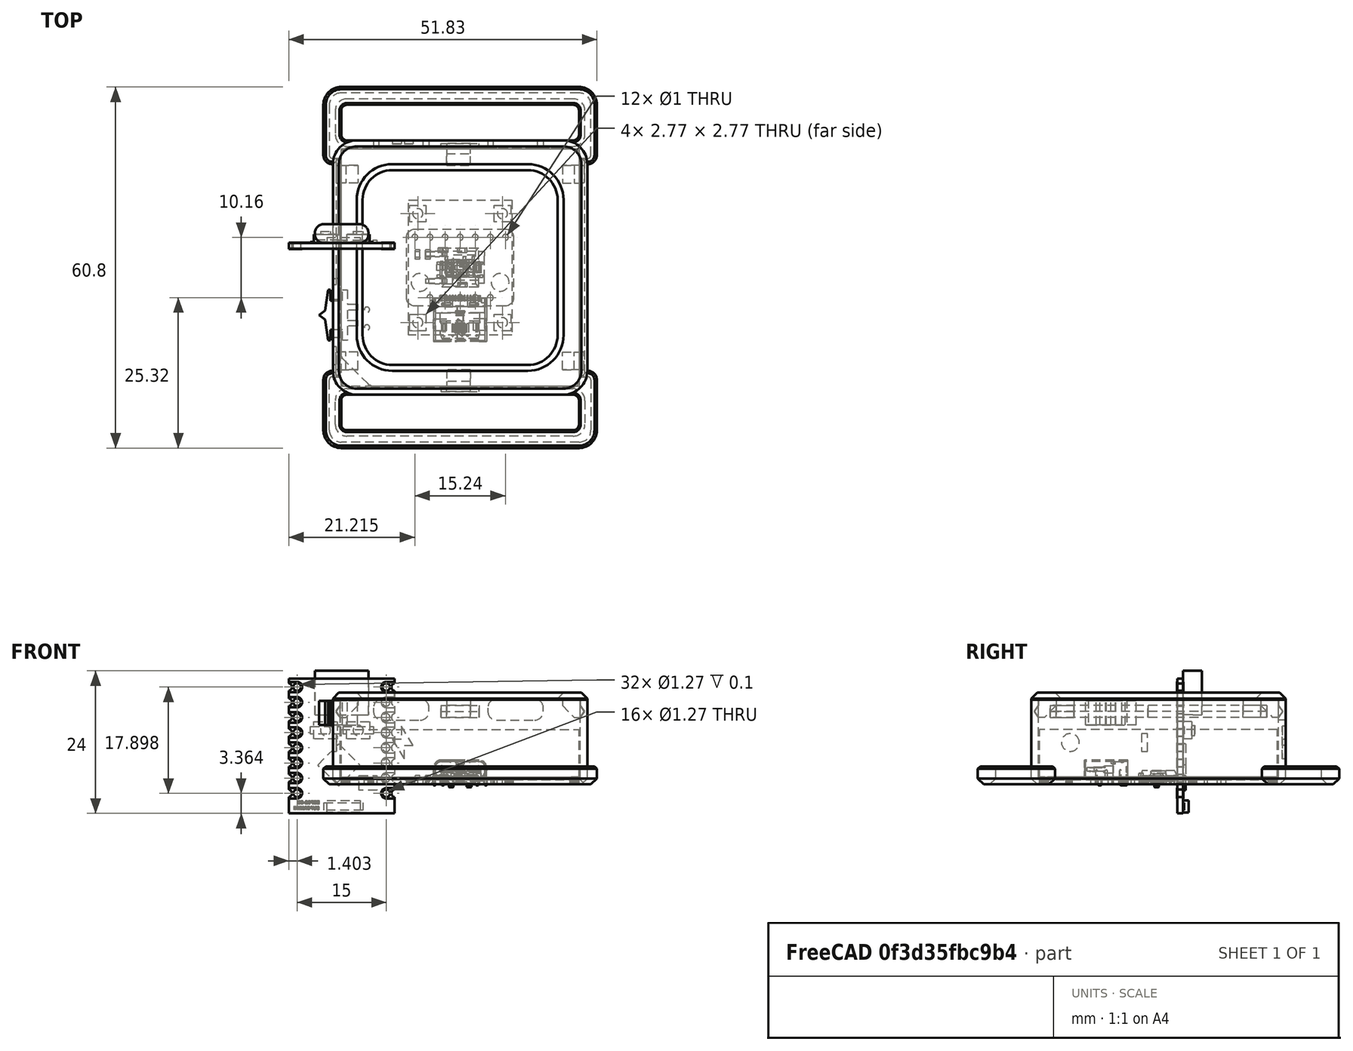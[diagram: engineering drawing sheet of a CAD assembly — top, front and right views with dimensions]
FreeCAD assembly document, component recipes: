
FREECAD ASSEMBLY — COMPONENT RECIPES ("tiny-slime-case")

This assembly document has 5 components, labeled P0..P4 below (a component is one placed body or linked part). 4 of them carry a construction recipe — the FreeCAD feature program that regenerates the part from scratch, quoted from this document or its linked companion documents; the rest are supplied as boundary geometry only. No exploded tour is included for this assembly.
COMPONENT P0 — recipe-attached ("Battery", modeled in this document).
Construction recipe (the document's own serialized feature program — sketch geometry with constraints, then the solid features built on it; lengths are millimeters unless a unit is written):

FEATURE [Sketcher::SketchObject] Sketch
  ArcFitTolerance = 1e-06
  AttachmentSupport = -> [XY_Plane]
  ExternalBSplineMaxDegree = 5
  ExternalBSplineTolerance = 0.0001
  FullyConstrained = true
  InternalTolerance = 1e-06
  InvalidShape = false
  MakeInternals = false
  MapMode = 5
  Support = -> [XY_Plane]
  TreeRank = 50
  ValidateShape = false
  sketch-geometry (4):
    g0: LineSegment StartX=-20 StartY=20 StartZ=0 EndX=20 EndY=20 EndZ=0
    g1: LineSegment StartX=20 StartY=20 StartZ=0 EndX=20 EndY=-20 EndZ=0
    g2: LineSegment StartX=20 StartY=-20 StartZ=0 EndX=-20 EndY=-20 EndZ=0
    g3: LineSegment StartX=-20 StartY=-20 StartZ=0 EndX=-20 EndY=20 EndZ=0
  constraints (11):
    c: Coincident(g0,g1)
    c: Coincident(g1,g2)
    c: Coincident(g2,g3)
    c: Coincident(g3,g0)
    c: Horizontal(g0)
    c: Horizontal(g2)
    c: Vertical(g1)
    c: Vertical(g3)
    c: DistanceY(g1,g1) = 40
    c: Equal(g1,g2)
    c: Symmetric(g1,g0,g-1)
FEATURE [PartDesign::Pad] Pad
  AddSubType = 0
  AlongSketchNormal = false
  AutoTaperInnerAngle = true
  CheckUpToFaceLimits = true
  ClaimChildren = false
  Direction = (0,0,1)
  Fit = 0
  FitJoin = 0
  InnerFit = 0
  InnerFitJoin = 0
  InvalidShape = false
  Length = 8
  Length2 = 10
  Linearize = true
  NewSolid = false
  Profile = -> Sketch
  ReferenceAxis = -> Sketch [N_Axis]
  Suppress = false
  TaperInnerAngle = 0
  TaperInnerAngleRev = 0
  TreeRank = 51
  Type = 0
  ValidateShape = false
  _ProfileBasedVersion = 1
FEATURE [PartDesign::Body] Body  label="Battery"
  AutoGroupSolids = false
  ClaimAllChildren = false
  ExportMode = 0
  Group = -> [Sketch,Pad]
  InvalidShape = false
  Origin = -> Origin008
  Placement = pos=(0,0,1.2) rot=(0,0,1;0rad)
  Tip = -> Pad
  TreeRank = 49
  ValidateShape = false
  _ExportChildren = -> [Pad]
  _GroupVersion = 1
COMPONENT P1 — recipe-attached ("Bottom", modeled in this document).
Construction recipe (the document's own serialized feature program — sketch geometry with constraints, then the solid features built on it; lengths are millimeters unless a unit is written):

FEATURE [Part::SubShapeBinder] Import  label="Import(Pad)"
  BindCopyOnChange = 0
  BindMode = 0
  ClaimChildren = false
  Context = -> Body001 [Import.]
  EdgeTolerance = 1e-06
  FillStyle = 0
  Fuse = false
  InvalidShape = false
  MakeFace = false
  MergeEdges = true
  OffsetFill = false
  OffsetIntersection = false
  OffsetJoinType = 0
  OffsetOpenResult = false
  Outline = false
  PartialLoad = false
  Relative = true
  SplitEdges = false
  Support = -> [Body[Pad.]]
  TightBound = false
  TreeRank = 62
  ValidateShape = false
  _Version = 8
FEATURE [Sketcher::SketchObject] Sketch001
  ArcFitTolerance = 1e-06
  AttachmentSupport = -> [Import]
  ExternalBSplineMaxDegree = 5
  ExternalBSplineTolerance = 0.0001
  ExternalGeometry = -> [Import]
  FullyConstrained = true
  InternalTolerance = 1e-06
  InvalidShape = false
  MakeInternals = false
  MapMode = 5
  Placement = pos=(0,0,1.2) rot=(1,0,0;3.14159rad)
  Support = -> [Import]
  TreeRank = 63
  ValidateShape = false
  sketch-geometry (4):
    g0: LineSegment StartX=-21.4 StartY=21.4 StartZ=0 EndX=21.4 EndY=21.4 EndZ=0
    g1: LineSegment StartX=21.4 StartY=21.4 StartZ=0 EndX=21.4 EndY=-21.4 EndZ=0
    g2: LineSegment StartX=21.4 StartY=-21.4 StartZ=0 EndX=-21.4 EndY=-21.4 EndZ=0
    g3: LineSegment StartX=-21.4 StartY=-21.4 StartZ=0 EndX=-21.4 EndY=21.4 EndZ=0
  constraints (11):
    c: Coincident(g0,g1)
    c: Coincident(g1,g2)
    c: Coincident(g2,g3)
    c: Coincident(g3,g0)
    c: Horizontal(g0)
    c: Horizontal(g2)
    c: Vertical(g1)
    c: Vertical(g3)
    c: Symmetric(g1,g0,g-1)
    c: Equal(g1,g0)
    c: DistanceY(g-3,g0) = 1.4
FEATURE [PartDesign::Pad] Pad001
  AddSubType = 0
  AlongSketchNormal = false
  AutoTaperInnerAngle = true
  CheckUpToFaceLimits = true
  ClaimChildren = false
  Direction = (0,0,-1)
  Fit = 0
  FitJoin = 0
  InnerFit = 0
  InnerFitJoin = 0
  InvalidShape = false
  Length = 1.2
  Length2 = 10
  Linearize = true
  NewSolid = false
  Profile = -> Sketch001
  ReferenceAxis = -> Sketch001 [N_Axis]
  Suppress = false
  TaperInnerAngle = 0
  TaperInnerAngleRev = 0
  TreeRank = 64
  Type = 0
  ValidateShape = false
  _ProfileBasedVersion = 1
FEATURE [Sketcher::SketchObject] Sketch002
  ArcFitTolerance = 1e-06
  AttachmentSupport = -> [Pad001]
  ExternalBSplineMaxDegree = 5
  ExternalBSplineTolerance = 0.0001
  ExternalGeometry = -> [Pad001]
  FullyConstrained = true
  InternalTolerance = 1e-06
  InvalidShape = false
  MakeInternals = false
  MapMode = 5
  Placement = pos=(0,0,1.2) rot=(0,0,1;0rad)
  Support = -> [Pad001]
  TreeRank = 65
  ValidateShape = false
  sketch-geometry (4):
    g0: LineSegment StartX=-20.2 StartY=20.2 StartZ=0 EndX=20.2 EndY=20.2 EndZ=0
    g1: LineSegment StartX=20.2 StartY=20.2 StartZ=0 EndX=20.2 EndY=-20.2 EndZ=0
    g2: LineSegment StartX=20.2 StartY=-20.2 StartZ=0 EndX=-20.2 EndY=-20.2 EndZ=0
    g3: LineSegment StartX=-20.2 StartY=-20.2 StartZ=0 EndX=-20.2 EndY=20.2 EndZ=0
  constraints (11):
    c: Coincident(g0,g1)
    c: Coincident(g1,g2)
    c: Coincident(g2,g3)
    c: Coincident(g3,g0)
    c: Horizontal(g0)
    c: Horizontal(g2)
    c: Vertical(g1)
    c: Vertical(g3)
    c: Symmetric(g1,g0,g-1)
    c: Equal(g0,g3)
    c: DistanceY(g0,g-4) = 1.2
FEATURE [PartDesign::SubShapeBinder] Import001  label="Import001(COMPOUND)"
  BindCopyOnChange = 0
  BindMode = 0
  ClaimChildren = false
  Context = -> Body001 [Import001.]
  EdgeTolerance = 1e-06
  FillStyle = 0
  Fuse = false
  InvalidShape = false
  MakeFace = false
  MergeEdges = true
  OffsetFill = false
  OffsetIntersection = false
  OffsetJoinType = 0
  OffsetOpenResult = false
  Outline = false
  PartialLoad = false
  Relative = true
  SplitEdges = false
  Support = -> [Part007[Part.Compound.Face247]]
  TightBound = false
  TreeRank = 67
  ValidateShape = false
  _Version = 8
FEATURE [PartDesign::Pad] Pad002
  AddSubType = 0
  AlongSketchNormal = false
  AutoTaperInnerAngle = true
  BaseFeature = -> Pad001
  CheckUpToFaceLimits = true
  ClaimChildren = false
  Direction = (0,0,1)
  Fit = 0
  FitJoin = 0
  InnerFit = 0
  InnerFitJoin = 0
  InvalidShape = false
  Length = 10
  Length2 = 10
  Linearize = true
  NewSolid = false
  Offset = -0.1
  Profile = -> Sketch002
  ReferenceAxis = -> Sketch002 [N_Axis]
  Suppress = false
  TaperInnerAngle = 0
  TaperInnerAngleRev = 0
  TreeRank = 66
  Type = 3
  UpToFace = -> Import001
  ValidateShape = false
  _ProfileBasedVersion = 1
FEATURE [Part::SubShapeBinder] Import002  label="Import002(COMPOUND)"
  BindCopyOnChange = 0
  BindMode = 0
  ClaimChildren = false
  Context = -> Body001 [Import002.]
  EdgeTolerance = 1e-06
  FillStyle = 0
  Fuse = false
  InvalidShape = false
  MakeFace = false
  MergeEdges = true
  OffsetFill = false
  OffsetIntersection = false
  OffsetJoinType = 0
  OffsetOpenResult = false
  Outline = false
  PartialLoad = false
  Relative = true
  SplitEdges = false
  Support = -> [Part007[Part002.Compound001.]]
  TightBound = false
  TreeRank = 69
  ValidateShape = false
  _Version = 8
FEATURE [Part::SubShapeBinder] Import003  label="Import003(COMPOUND)"
  BindCopyOnChange = 0
  BindMode = 0
  ClaimChildren = false
  Context = -> Body001 [Import003.]
  EdgeTolerance = 1e-06
  FillStyle = 0
  Fuse = false
  InvalidShape = false
  MakeFace = false
  MergeEdges = true
  OffsetFill = false
  OffsetIntersection = false
  OffsetJoinType = 0
  OffsetOpenResult = false
  Outline = false
  PartialLoad = false
  Relative = true
  SplitEdges = false
  Support = -> [Part007[Part.Compound.]]
  TightBound = false
  TreeRank = 70
  ValidateShape = false
  _Version = 8
FEATURE [Sketcher::SketchObject] Sketch003
  ArcFitTolerance = 1e-06
  AttachmentSupport = -> [Pad002]
  ExternalBSplineMaxDegree = 5
  ExternalBSplineTolerance = 0.0001
  ExternalGeometry = -> [Import002,Import003]
  FullyConstrained = true
  InternalTolerance = 1e-06
  InvalidShape = false
  MakeInternals = false
  MapMode = 5
  Placement = pos=(0,21.4,0) rot=(0,0.707107,0.707107;3.14159rad)
  Support = -> [Pad002]
  TreeRank = 68
  ValidateShape = false
  sketch-geometry (22):
    g0: ArcOfCircle CenterX=6.7254 CenterY=12.8646 CenterZ=0 NormalX=0 NormalY=0 NormalZ=1 AngleXU=0 Radius=1.4954 StartAngle=1.5708 EndAngle=3.14159
    g1: LineSegment StartX=6.7254 StartY=14.36 StartZ=0 EndX=13.0746 EndY=14.36 EndZ=0
    g2: ArcOfCircle CenterX=13.0746 CenterY=12.8646 CenterZ=0 NormalX=0 NormalY=0 NormalZ=1 AngleXU=0 Radius=1.4954 StartAngle=0 EndAngle=1.5708
    g3: LineSegment StartX=14.57 StartY=12.8646 StartZ=0 EndX=14.57 EndY=12.2954 EndZ=0
    g4: ArcOfCircle CenterX=13.0746 CenterY=12.2954 CenterZ=0 NormalX=0 NormalY=0 NormalZ=1 AngleXU=0 Radius=1.4954 StartAngle=4.71239 EndAngle=6.28319
    g5: LineSegment StartX=13.0746 StartY=10.8 StartZ=0 EndX=6.7254 EndY=10.8 EndZ=0
    g6: ArcOfCircle CenterX=6.7254 CenterY=12.2954 CenterZ=0 NormalX=0 NormalY=0 NormalZ=1 AngleXU=0 Radius=1.4954 StartAngle=3.14159 EndAngle=4.71239
    g7: LineSegment StartX=5.23 StartY=12.2954 StartZ=0 EndX=5.23 EndY=12.8646 EndZ=0
    g8: GeomPoint [constr] X=5.23 Y=14.36 Z=0
    g9: GeomPoint [constr] X=14.57 Y=10.8 Z=0
    g10: ArcOfCircle CenterX=-12.508 CenterY=12.8646 CenterZ=0 NormalX=0 NormalY=0 NormalZ=1 AngleXU=0 Radius=1.4954 StartAngle=1.5708 EndAngle=3.14159
    g11: LineSegment StartX=-12.508 StartY=14.36 StartZ=0 EndX=-6.15878 EndY=14.36 EndZ=0
    g12: ArcOfCircle CenterX=-6.15878 CenterY=12.8646 CenterZ=0 NormalX=0 NormalY=0 NormalZ=1 AngleXU=0 Radius=1.4954 StartAngle=0 EndAngle=1.5708
    g13: LineSegment StartX=-4.66338 StartY=12.8646 StartZ=0 EndX=-4.66338 EndY=12.2954 EndZ=0
    g14: ArcOfCircle CenterX=-6.15878 CenterY=12.2954 CenterZ=0 NormalX=0 NormalY=0 NormalZ=1 AngleXU=0 Radius=1.4954 StartAngle=4.71239 EndAngle=6.28319
    g15: LineSegment StartX=-6.15878 StartY=10.8 StartZ=0 EndX=-12.508 EndY=10.8 EndZ=0
    g16: ArcOfCircle CenterX=-12.508 CenterY=12.2954 CenterZ=0 NormalX=0 NormalY=0 NormalZ=1 AngleXU=0 Radius=1.4954 StartAngle=3.14159 EndAngle=4.71239
    g17: LineSegment StartX=-14.0034 StartY=12.2954 StartZ=0 EndX=-14.0034 EndY=12.8646 EndZ=0
    g18: GeomPoint [constr] X=-14.0034 Y=14.36 Z=0
    g19: GeomPoint [constr] X=-4.66338 Y=10.8 Z=0
    g20: LineSegment [constr] StartX=-18.2334 StartY=10.9 StartZ=0 EndX=-12.508 EndY=12.2954 EndZ=0
    g21: LineSegment [constr] StartX=-6.15878 StartY=12.2954 StartZ=0 EndX=-0.433383 EndY=10.9 EndZ=0
  constraints (49):
    c: Tangent(g0,g1) = 1.5708
    c: Tangent(g1,g2) = 1.5708
    c: Tangent(g2,g3) = 1.5708
    c: Tangent(g3,g4) = 1.5708
    c: Tangent(g4,g5) = 1.5708
    c: Tangent(g5,g6) = 1.5708
    c: Tangent(g6,g7) = 1.5708
    c: Tangent(g7,g0) = 1.5708
    c: Horizontal(g1)
    c: Horizontal(g5)
    c: Vertical(g3)
    c: Vertical(g7)
    c: Equal(g4,g6)
    c: PointOnObject(g8,g1)
    c: PointOnObject(g8,g7)
    c: PointOnObject(g9,g3)
    c: PointOnObject(g9,g5)
    c: Coincident(g4,g-13)
    c: Coincident(g-11,g2)
    c: Coincident(g0,g-9)
    c: DistanceY(g-10,g0) = 0.2
    c: Tangent(g10,g11) = 1.5708
    c: Tangent(g11,g12) = 1.5708
    c: Tangent(g12,g13) = 1.5708
    c: Tangent(g13,g14) = 1.5708
    c: Tangent(g14,g15) = 1.5708
    c: Tangent(g15,g16) = 1.5708
    c: Tangent(g16,g17) = 1.5708
    c: Tangent(g17,g10) = 1.5708
    c: Horizontal(g11)
    c: Horizontal(g15)
    c: Vertical(g13)
    c: Vertical(g17)
    c: Equal(g10,g12)
    c: Equal(g12,g14)
    c: Equal(g14,g16)
    c: PointOnObject(g18,g11)
    c: PointOnObject(g18,g17)
    c: PointOnObject(g19,g13)
    c: PointOnObject(g19,g15)
    c: Equal(g12,g2)
    c: Equal(g13,g3)
    c: Equal(g1,g11)
    c: Horizontal(g14,g6)
    c: Coincident(g20,g16)
    c: Coincident(g21,g14)
    c: Coincident(g21,g-18)
    c: Equal(g21,g20)
    c: Coincident(g-19,g20)
FEATURE [Part::SubShapeBinder] Import004  label="Import004(COMPOUND)"
  BindCopyOnChange = 0
  BindMode = 0
  ClaimChildren = false
  Context = -> Body001 [Import004.]
  EdgeTolerance = 1e-06
  FillStyle = 0
  Fuse = false
  InvalidShape = false
  MakeFace = false
  MergeEdges = true
  OffsetFill = false
  OffsetIntersection = false
  OffsetJoinType = 0
  OffsetOpenResult = false
  Outline = false
  PartialLoad = false
  Relative = true
  SplitEdges = false
  Support = -> [Part007[Part004.Compound002.]]
  TightBound = false
  TreeRank = 71
  ValidateShape = false
  _Version = 8
FEATURE [PartDesign::Pocket] Pocket
  AddSubType = 1
  AlongSketchNormal = false
  AutoTaperInnerAngle = true
  BaseFeature = -> Pad002
  CheckUpToFaceLimits = true
  ClaimChildren = false
  Direction = (0,-1,2e-16)
  Fit = 0
  FitJoin = 0
  InnerFit = 0
  InnerFitJoin = 0
  InvalidShape = false
  Length = 5
  Length2 = 10
  Linearize = true
  NewSolid = false
  Profile = -> Sketch003
  ReferenceAxis = -> Sketch003 [N_Axis]
  Suppress = false
  TaperInnerAngle = 0
  TaperInnerAngleRev = 0
  TreeRank = 72
  Type = 2
  ValidateShape = false
  _ProfileBasedVersion = 1
  _Version = 1
FEATURE [Part::SubShapeBinder] Import005  label="Import005(SOLID)"
  BindCopyOnChange = 0
  BindMode = 0
  ClaimChildren = false
  Context = -> Body001 [Import005.]
  EdgeTolerance = 1e-06
  FillStyle = 0
  Fuse = false
  InvalidShape = false
  MakeFace = false
  MergeEdges = true
  OffsetFill = false
  OffsetIntersection = false
  OffsetJoinType = 0
  OffsetOpenResult = false
  Outline = false
  PartialLoad = false
  Relative = true
  SplitEdges = false
  Support = -> [Part007[Part006.Solid002.]]
  TightBound = false
  TreeRank = 74
  ValidateShape = false
  _Version = 8
FEATURE [Sketcher::SketchObject] Sketch004
  ArcFitTolerance = 1e-06
  AttachmentSupport = -> [Pocket]
  ExternalBSplineMaxDegree = 5
  ExternalBSplineTolerance = 0.0001
  ExternalGeometry = -> [Import005,Pocket]
  FullyConstrained = true
  InternalTolerance = 1e-06
  InvalidShape = false
  MakeInternals = false
  MapMode = 5
  Placement = pos=(0,-3.1e-15,14.26) rot=(0,0,1;0rad)
  Support = -> [Pocket]
  TreeRank = 73
  ValidateShape = false
  sketch-geometry (7):
    g0: LineSegment [constr] StartX=-18.2744 StartY=-7.3656 StartZ=0 EndX=-16.6844 EndY=-5.2456 EndZ=0
    g1: LineSegment [constr] StartX=-18.2744 StartY=-7.3656 StartZ=0 EndX=-18.2744 EndY=-9.8256 EndZ=0
    g2: LineSegment [constr] StartX=-18.2744 StartY=-9.8256 StartZ=0 EndX=-16.6844 EndY=-11.9456 EndZ=0
    g3: LineSegment StartX=-21.4 StartY=-5.3656 StartZ=0 EndX=-20.2 EndY=-5.3656 EndZ=0
    g4: LineSegment StartX=-20.2 StartY=-5.3656 StartZ=0 EndX=-20.2 EndY=-11.8256 EndZ=0
    g5: LineSegment StartX=-20.2 StartY=-11.8256 StartZ=0 EndX=-21.4 EndY=-11.8256 EndZ=0
    g6: LineSegment StartX=-21.4 StartY=-11.8256 StartZ=0 EndX=-21.4 EndY=-5.3656 EndZ=0
  constraints (19):
    c: Coincident(g0,g-5)
    c: Coincident(g0,g-3)
    c: Coincident(g1,g-5)
    c: Vertical(g1)
    c: Coincident(g2,g1)
    c: Coincident(g2,g-4)
    c: Equal(g2,g0)
    c: Coincident(g3,g4)
    c: Coincident(g4,g5)
    c: Coincident(g5,g6)
    c: Coincident(g6,g3)
    c: Horizontal(g3)
    c: Horizontal(g5)
    c: Vertical(g4)
    c: Vertical(g6)
    c: PointOnObject(g3,g-7)
    c: PointOnObject(g4,g-8)
    c: DistanceY(g-5,g3) = 2
    c: DistanceY(g4,g1) = 2
FEATURE [PartDesign::SubShapeBinder] Import006  label="Import006(tiny-slime PCB)"
  BindCopyOnChange = 0
  BindMode = 0
  ClaimChildren = false
  Context = -> Body001 [Import006.]
  EdgeTolerance = 1e-06
  FillStyle = 0
  Fuse = false
  InvalidShape = false
  MakeFace = false
  MergeEdges = true
  OffsetFill = false
  OffsetIntersection = false
  OffsetJoinType = 0
  OffsetOpenResult = false
  Outline = false
  PartialLoad = false
  Relative = true
  SplitEdges = false
  Support = -> [Part007[Solid003.Face5]]
  TightBound = false
  TreeRank = 76
  ValidateShape = false
  _Version = 8
FEATURE [PartDesign::Pocket] Pocket001
  AddSubType = 1
  AlongSketchNormal = false
  AutoTaperInnerAngle = true
  BaseFeature = -> Pocket
  CheckUpToFaceLimits = true
  ClaimChildren = false
  Direction = (0,2e-16,-1)
  Fit = 0
  FitJoin = 0
  InnerFit = 0
  InnerFitJoin = 0
  InvalidShape = false
  Length = 0
  Length2 = 10
  Linearize = true
  NewSolid = false
  Profile = -> Sketch004
  ReferenceAxis = -> Sketch004 [N_Axis]
  Suppress = false
  TaperInnerAngle = 0
  TaperInnerAngleRev = 0
  TreeRank = 75
  Type = 3
  UpToFace = -> Import006
  ValidateShape = false
  _ProfileBasedVersion = 1
  _Version = 1
FEATURE [Sketcher::SketchObject] Sketch006
  ArcFitTolerance = 1e-06
  AttachmentOffset = pos=(0,0,2) rot=(0,0,1;0rad)
  AttachmentSupport = -> [Pocket001]
  ExternalBSplineMaxDegree = 5
  ExternalBSplineTolerance = 0.0001
  ExternalGeometry = -> [Pocket001]
  FullyConstrained = true
  InternalTolerance = 1e-06
  InvalidShape = false
  MakeInternals = false
  MapMode = 5
  Placement = pos=(0,18.2,4e-16) rot=(1,0,0;1.5708rad)
  Support = -> [Pocket001]
  TreeRank = 92
  ValidateShape = false
  sketch-geometry (3):
    g0: LineSegment StartX=20.2 StartY=13.26 StartZ=0 EndX=20.9002 EndY=12.26 EndZ=0
    g1: LineSegment StartX=20.9002 StartY=12.26 StartZ=0 EndX=20.2 EndY=11.26 EndZ=0
    g2: LineSegment StartX=20.2 StartY=11.26 StartZ=0 EndX=20.2 EndY=13.26 EndZ=0
  constraints (9):
    c: PointOnObject(g0,g-3)
    c: Coincident(g0,g1)
    c: PointOnObject(g1,g-3)
    c: Coincident(g1,g2)
    c: Coincident(g2,g0)
    c: Equal(g0,g1)
    c: DistanceY(g0,g-3) = 1
    c: DistanceY(g1,g0) = 2
    c: Angle(g0,g1) = 1.91986
FEATURE [PartDesign::Pocket] Pocket002
  AddSubType = 1
  AlongSketchNormal = false
  AutoTaperInnerAngle = true
  BaseFeature = -> Pocket001
  CheckUpToFaceLimits = true
  ClaimChildren = false
  Direction = (0,1,-2e-16)
  Fit = 0
  FitJoin = 0
  InnerFit = 0
  InnerFitJoin = 0
  InvalidShape = false
  Length = 0
  Length2 = 10
  Linearize = true
  NewSolid = false
  Offset = 2
  Profile = -> Sketch006
  ReferenceAxis = -> Sketch006 [N_Axis]
  Reversed = true
  Suppress = false
  TaperInnerAngle = 0
  TaperInnerAngleRev = 0
  TreeRank = 93
  Type = 3
  UpToFace = -> Pocket001 [Face16]
  ValidateShape = false
  _ProfileBasedVersion = 1
  _Version = 1
FEATURE [Sketcher::SketchObject] Sketch007
  ArcFitTolerance = 1e-06
  AttachmentOffset = pos=(0,0,17) rot=(0,0,1;0rad)
  AttachmentSupport = -> [Pocket002]
  ExternalBSplineMaxDegree = 5
  ExternalBSplineTolerance = 0.0001
  ExternalGeometry = -> [Pocket002]
  FullyConstrained = true
  InternalTolerance = 1e-06
  InvalidShape = false
  MakeInternals = false
  MapMode = 5
  Placement = pos=(-3.2,0,0) rot=(0.57735,0.57735,0.57735;2.0944rad)
  Support = -> [Pocket002]
  TreeRank = 94
  ValidateShape = false
  sketch-geometry (6):
    g0: LineSegment StartX=20.2 StartY=13.26 StartZ=0 EndX=20.9002 EndY=12.26 EndZ=0
    g1: LineSegment StartX=20.9002 StartY=12.26 StartZ=0 EndX=20.2 EndY=11.26 EndZ=0
    g2: LineSegment StartX=20.2 StartY=11.26 StartZ=0 EndX=20.2 EndY=13.26 EndZ=0
    g3: LineSegment StartX=-20.2 StartY=13.26 StartZ=0 EndX=-20.9002 EndY=12.26 EndZ=0
    g4: LineSegment StartX=-20.9002 StartY=12.26 StartZ=0 EndX=-20.2 EndY=11.26 EndZ=0
    g5: LineSegment StartX=-20.2 StartY=11.26 StartZ=0 EndX=-20.2 EndY=13.26 EndZ=0
  constraints (18):
    c: PointOnObject(g0,g-3)
    c: Coincident(g0,g1)
    c: PointOnObject(g1,g-3)
    c: Coincident(g1,g2)
    c: Coincident(g2,g0)
    c: Equal(g0,g1)
    c: Angle(g0,g1) = 1.91986
    c: DistanceY(g1,g0) = 2
    c: DistanceY(g0,g-3) = 1
    c: PointOnObject(g3,g-4)
    c: Coincident(g3,g4)
    c: PointOnObject(g4,g-4)
    c: Coincident(g4,g5)
    c: Coincident(g5,g3)
    c: Equal(g3,g4)
    c: DistanceY(g5,g5) = 2
    c: DistanceY(g3,g-4) = 1
    c: Angle(g4,g3) = 1.91986
FEATURE [PartDesign::Pocket] Pocket003
  AddSubType = 1
  AlongSketchNormal = false
  AutoTaperInnerAngle = true
  BaseFeature = -> Pocket002
  CheckUpToFaceLimits = true
  ClaimChildren = false
  Direction = (-1,0,0)
  Fit = 0
  FitJoin = 0
  InnerFit = 0
  InnerFitJoin = 0
  InvalidShape = false
  Length = 0
  Length2 = 10
  Linearize = true
  NewSolid = false
  Offset = 17
  Profile = -> Sketch007
  ReferenceAxis = -> Sketch007 [N_Axis]
  Reversed = true
  Suppress = false
  TaperInnerAngle = 0
  TaperInnerAngleRev = 0
  TreeRank = 95
  Type = 3
  UpToFace = -> Pocket002 [Face17]
  ValidateShape = false
  _ProfileBasedVersion = 1
  _Version = 1
FEATURE [Sketcher::SketchObject] Sketch008
  ArcFitTolerance = 1e-06
  AttachmentOffset = pos=(0,0,2) rot=(0,0,1;0rad)
  AttachmentSupport = -> [Pocket003]
  ExternalBSplineMaxDegree = 5
  ExternalBSplineTolerance = 0.0001
  ExternalGeometry = -> [Pocket003]
  FullyConstrained = true
  InternalTolerance = 1e-06
  InvalidShape = false
  MakeInternals = false
  MapMode = 5
  Placement = pos=(0,18.2,4e-16) rot=(1,0,0;1.5708rad)
  Support = -> [Pocket003]
  TreeRank = 96
  ValidateShape = false
  sketch-geometry (3):
    g0: LineSegment StartX=-20.2 StartY=13.26 StartZ=0 EndX=-20.9002 EndY=12.26 EndZ=0
    g1: LineSegment StartX=-20.9002 StartY=12.26 StartZ=0 EndX=-20.2 EndY=11.26 EndZ=0
    g2: LineSegment StartX=-20.2 StartY=11.26 StartZ=0 EndX=-20.2 EndY=13.26 EndZ=0
  constraints (9):
    c: PointOnObject(g0,g-3)
    c: Coincident(g0,g1)
    c: PointOnObject(g1,g-3)
    c: Coincident(g1,g2)
    c: Coincident(g2,g0)
    c: Equal(g0,g1)
    c: Angle(g1,g0) = 1.91986
    c: DistanceY(g0,g-3) = 1
    c: DistanceY(g2,g2) = 2
FEATURE [PartDesign::Pocket] Pocket004
  AddSubType = 1
  AlongSketchNormal = false
  AutoTaperInnerAngle = true
  BaseFeature = -> Pocket003
  CheckUpToFaceLimits = true
  ClaimChildren = false
  Direction = (0,1,-2e-16)
  Fit = 0
  FitJoin = 0
  InnerFit = 0
  InnerFitJoin = 0
  InvalidShape = false
  Length = 20
  Length2 = 10
  Linearize = true
  NewSolid = false
  Profile = -> Sketch008
  ReferenceAxis = -> Sketch008 [N_Axis]
  Reversed = true
  Suppress = false
  TaperInnerAngle = 0
  TaperInnerAngleRev = 0
  TreeRank = 97
  Type = 0
  ValidateShape = false
  _ProfileBasedVersion = 1
  _Version = 1
FEATURE [Sketcher::SketchObject] Sketch009
  ArcFitTolerance = 1e-06
  AttachmentOffset = pos=(0,0,2) rot=(0,0,1;0rad)
  AttachmentSupport = -> [Pocket004]
  ExternalBSplineMaxDegree = 5
  ExternalBSplineTolerance = 0.0001
  ExternalGeometry = -> [Pocket004]
  FullyConstrained = true
  InternalTolerance = 1e-06
  InvalidShape = false
  MakeInternals = false
  MapMode = 5
  Placement = pos=(0,-18.2,-4e-16) rot=(0,0.707107,0.707107;3.14159rad)
  Support = -> [Pocket004]
  TreeRank = 98
  ValidateShape = false
  sketch-geometry (3):
    g0: LineSegment StartX=20.2 StartY=13.26 StartZ=0 EndX=20.9002 EndY=12.26 EndZ=0
    g1: LineSegment StartX=20.9002 StartY=12.26 StartZ=0 EndX=20.2 EndY=11.26 EndZ=0
    g2: LineSegment StartX=20.2 StartY=11.26 StartZ=0 EndX=20.2 EndY=13.26 EndZ=0
  constraints (9):
    c: PointOnObject(g0,g-3)
    c: Coincident(g0,g1)
    c: PointOnObject(g1,g-3)
    c: Coincident(g1,g2)
    c: Coincident(g2,g0)
    c: Equal(g1,g0)
    c: DistanceY(g2,g2) = 2
    c: DistanceY(g0,g-3) = 1
    c: Angle(g0,g1) = 1.91986
FEATURE [PartDesign::Pocket] Pocket005
  AddSubType = 1
  AlongSketchNormal = false
  AutoTaperInnerAngle = true
  BaseFeature = -> Pocket004
  CheckUpToFaceLimits = true
  ClaimChildren = false
  Direction = (0,-1,2e-16)
  Fit = 0
  FitJoin = 0
  InnerFit = 0
  InnerFitJoin = 0
  InvalidShape = false
  Length = 4
  Length2 = 10
  Linearize = true
  NewSolid = false
  Profile = -> Sketch009
  ReferenceAxis = -> Sketch009 [N_Axis]
  Reversed = true
  Suppress = false
  TaperInnerAngle = 0
  TaperInnerAngleRev = 0
  TreeRank = 99
  Type = 0
  ValidateShape = false
  _ProfileBasedVersion = 1
  _Version = 1
FEATURE [PartDesign::Fillet] Fillet001
  AddSubType = 0
  Base = -> Pocket005 [Edge57,Edge58,Edge74,Edge68]
  BaseFeature = -> Pocket005
  InvalidShape = false
  NewSolid = false
  Radius = 1.5
  SupportTransform = false
  Suppress = false
  TreeRank = 126
  UseAllEdges = false
  ValidateShape = true
FEATURE [PartDesign::Fillet] Fillet002
  AddSubType = 0
  Base = -> Fillet001 [Edge40,Edge44,Edge56,Edge48]
  BaseFeature = -> Fillet001
  InvalidShape = false
  NewSolid = false
  Radius = 4
  SupportTransform = false
  Suppress = false
  TreeRank = 127
  UseAllEdges = false
  ValidateShape = true
FEATURE [Sketcher::SketchObject] Sketch015
  ArcFitTolerance = 1e-06
  AttachmentSupport = -> [Fillet002]
  ExternalBSplineMaxDegree = 5
  ExternalBSplineTolerance = 0.0001
  ExternalGeometry = -> [Fillet002]
  FullyConstrained = true
  InternalTolerance = 1e-06
  InvalidShape = false
  MakeInternals = false
  MapMode = 5
  Placement = pos=(0,0,0) rot=(1,0,0;3.14159rad)
  Support = -> [Fillet002]
  TreeRank = 128
  ValidateShape = false
  sketch-geometry (12):
    g0: LineSegment StartX=-20 StartY=21.4 StartZ=0 EndX=20 EndY=21.4 EndZ=0
    g1: LineSegment StartX=20 StartY=21.4 StartZ=0 EndX=20 EndY=27.4 EndZ=0
    g2: LineSegment StartX=20 StartY=27.4 StartZ=0 EndX=-20 EndY=27.4 EndZ=0
    g3: LineSegment StartX=-20 StartY=27.4 StartZ=0 EndX=-20 EndY=21.4 EndZ=0
    g4: LineSegment StartX=17.4 StartY=21.3 StartZ=0 EndX=-17.4 EndY=21.3 EndZ=0
    g5: ArcOfCircle CenterX=17.4 CenterY=17.4 CenterZ=0 NormalX=0 NormalY=0 NormalZ=1 AngleXU=0 Radius=3.9 StartAngle=0 EndAngle=1.5708
    g6: ArcOfCircle CenterX=-17.4 CenterY=17.4 CenterZ=0 NormalX=0 NormalY=0 NormalZ=1 AngleXU=0 Radius=3.9 StartAngle=1.5708 EndAngle=3.14159
    g7: LineSegment StartX=-21.3 StartY=17.4 StartZ=0 EndX=-23 EndY=17.4 EndZ=0
    g8: LineSegment StartX=-23 StartY=17.4 StartZ=0 EndX=-23 EndY=30.4 EndZ=0
    g9: LineSegment StartX=-23 StartY=30.4 StartZ=0 EndX=23 EndY=30.4 EndZ=0
    g10: LineSegment StartX=23 StartY=30.4 StartZ=0 EndX=23 EndY=17.4 EndZ=0
    g11: LineSegment StartX=21.3 StartY=17.4 StartZ=0 EndX=23 EndY=17.4 EndZ=0
  constraints (35):
    c: Coincident(g0,g1)
    c: Coincident(g1,g2)
    c: Coincident(g2,g3)
    c: Coincident(g3,g0)
    c: Horizontal(g0)
    c: Vertical(g1)
    c: Vertical(g3)
    c: DistanceY(g1,g1) = 6
    c: DistanceX(g2,g2) = 40
    c: Symmetric(g1,g2,g-2)
    c: PointOnObject(g-4,g0)
    c: Horizontal(g4)
    c: DistanceY(g4,g-4) = 0.1
    c: Vertical(g4,g-4)
    c: Vertical(g4,g-5)
    c: Coincident(g5,g-5)
    c: Coincident(g5,g4)
    c: Horizontal(g5,g-5)
    c: Coincident(g6,g-3)
    c: Coincident(g6,g4)
    c: Horizontal(g6,g-3)
    c: Coincident(g7,g6)
    c: Horizontal(g7)
    c: DistanceX(g7,g0) = 3
    c: Coincident(g8,g7)
    c: Vertical(g8)
    c: DistanceY(g2,g8) = 3
    c: Coincident(g9,g8)
    c: Horizontal(g9)
    c: DistanceX(g1,g9) = 3
    c: Coincident(g10,g9)
    c: Vertical(g10)
    c: Coincident(g11,g5)
    c: Coincident(g11,g10)
    c: Horizontal(g11)
FEATURE [PartDesign::Pad] Pad009
  AddSubType = 0
  AlongSketchNormal = false
  AutoTaperInnerAngle = true
  BaseFeature = -> Fillet002
  CheckUpToFaceLimits = true
  ClaimChildren = false
  Direction = (0,0,-1)
  Fit = 0
  FitJoin = 0
  InnerFit = 0
  InnerFitJoin = 0
  InvalidShape = false
  Length = 3
  Length2 = 10
  Linearize = true
  NewSolid = false
  Profile = -> Sketch015
  ReferenceAxis = -> Sketch015 [N_Axis]
  Refine = true
  Reversed = true
  Suppress = false
  TaperInnerAngle = 0
  TaperInnerAngleRev = 0
  TreeRank = 129
  Type = 0
  ValidateShape = true
  _ProfileBasedVersion = 1
FEATURE [PartDesign::Fillet] Fillet003
  AddSubType = 0
  Base = -> Pad009 [Edge122,Edge2]
  BaseFeature = -> Pad009
  InvalidShape = false
  NewSolid = false
  Radius = 1.5
  SupportTransform = false
  Suppress = false
  TreeRank = 130
  UseAllEdges = false
  ValidateShape = true
FEATURE [PartDesign::Fillet] Fillet004
  AddSubType = 0
  Base = -> Fillet003 [Edge77,Edge79,Edge78,Edge80]
  BaseFeature = -> Fillet003
  InvalidShape = false
  NewSolid = false
  Radius = 1
  SupportTransform = false
  Suppress = false
  TreeRank = 131
  UseAllEdges = false
  ValidateShape = true
FEATURE [PartDesign::Fillet] Fillet005
  AddSubType = 0
  Base = -> Fillet004 [Edge50,Edge54]
  BaseFeature = -> Fillet004
  InvalidShape = false
  NewSolid = false
  Radius = 3
  SupportTransform = false
  Suppress = false
  TreeRank = 132
  UseAllEdges = false
  ValidateShape = true
FEATURE [PartDesign::Mirrored] Mirrored003
  AddSubType = 0
  BaseFeature = -> Fillet005
  CopyShape = false
  InvalidShape = false
  MirrorPlane = -> Sketch015 [H_Axis]
  NewSolid = false
  OriginalSubs = -> [Pad009,Fillet003,Fillet004,Fillet005]
  Originals = -> [Pad009,Fillet003,Fillet004,Fillet005]
  ParallelTransform = true
  Refine = true
  SubTransform = true
  Suppress = false
  TreeRank = 133
  ValidateShape = true
  _Version = 3
FEATURE [PartDesign::Chamfer] Chamfer
  AddSubType = 0
  Angle = 45
  Base = -> Mirrored003 [Edge11,Edge73,Edge8,Edge21]
  BaseFeature = -> Mirrored003
  ChamferType = 0
  FlipDirection = false
  InvalidShape = false
  NewSolid = false
  Size = 1
  Size2 = 1
  SupportTransform = false
  Suppress = false
  TreeRank = 134
  UseAllEdges = false
  ValidateShape = true
FEATURE [PartDesign::Chamfer] Chamfer001
  AddSubType = 0
  Angle = 45
  Base = -> Chamfer [Edge130,Edge28]
  BaseFeature = -> Chamfer
  ChamferType = 0
  FlipDirection = false
  InvalidShape = false
  NewSolid = false
  Size = 0.3
  Size2 = 1
  SupportTransform = false
  Suppress = false
  TreeRank = 135
  UseAllEdges = false
  ValidateShape = true
FEATURE [PartDesign::Chamfer] Chamfer005
  AddSubType = 0
  Angle = 45
  Base = -> Chamfer001 [Edge259,Edge15]
  BaseFeature = -> Chamfer001
  ChamferType = 0
  FlipDirection = false
  InvalidShape = false
  NewSolid = false
  Size = 0.4
  Size2 = 1
  SupportTransform = false
  Suppress = false
  TreeRank = 146
  UseAllEdges = false
  ValidateShape = true
FEATURE [PartDesign::Chamfer] Chamfer002
  AddSubType = 0
  Angle = 45
  Base = -> Chamfer005 [Edge167,Edge108]
  BaseFeature = -> Chamfer005
  ChamferType = 0
  FlipDirection = false
  InvalidShape = false
  NewSolid = false
  Size = 1
  Size2 = 1
  SupportTransform = false
  Suppress = false
  TreeRank = 136
  UseAllEdges = false
  ValidateShape = true
FEATURE [Sketcher::SketchObject] Sketch017
  ArcFitTolerance = 1e-06
  AttachmentSupport = -> [Chamfer002]
  ExternalBSplineMaxDegree = 5
  ExternalBSplineTolerance = 0.0001
  ExternalGeometry = -> [Chamfer002]
  FullyConstrained = true
  InternalTolerance = 1e-06
  InvalidShape = false
  MakeInternals = false
  MapMode = 5
  Placement = pos=(0,21.4,-2.4e-15) rot=(0,0.707107,0.707107;3.14159rad)
  Support = -> [Chamfer002]
  TreeRank = 142
  ValidateShape = false
  sketch-geometry (8):
    g0: LineSegment StartX=7.9 StartY=6.55 StartZ=0 EndX=9.9 EndY=9.8 EndZ=0
    g1: LineSegment StartX=9.9 StartY=9.8 StartZ=0 EndX=9.9 EndY=7.55 EndZ=0
    g2: LineSegment StartX=9.9 StartY=7.55 StartZ=0 EndX=11.4 EndY=7.55 EndZ=0
    g3: LineSegment StartX=11.4 StartY=7.55 StartZ=0 EndX=9.4 EndY=4.3 EndZ=0
    g4: LineSegment StartX=9.4 StartY=4.3 StartZ=0 EndX=9.4 EndY=6.55 EndZ=0
    g5: LineSegment StartX=9.4 StartY=6.55 StartZ=0 EndX=7.9 EndY=6.55 EndZ=0
    g6: LineSegment [constr] StartX=6.7254 StartY=10.8 StartZ=0 EndX=9.9 EndY=9.8 EndZ=0
    g7: LineSegment [constr] StartX=9.9 StartY=9.8 StartZ=0 EndX=13.0746 EndY=10.8 EndZ=0
  constraints (22):
    c: Coincident(g0,g1)
    c: Vertical(g1)
    c: Coincident(g1,g2)
    c: Horizontal(g2)
    c: Coincident(g2,g3)
    c: Coincident(g3,g4)
    c: Vertical(g4)
    c: Coincident(g4,g5)
    c: Horizontal(g5)
    c: Coincident(g0,g5)
    c: Parallel(g3,g0)
    c: Equal(g4,g1)
    c: DistanceX(g5,g5) = 1.5
    c: DistanceY(g3,g0) = 5.5
    c: DistanceX(g0,g2) = 3.5
    c: Coincident(g6,g-3)
    c: Coincident(g6,g0)
    c: Coincident(g7,g0)
    c: Coincident(g7,g-3)
    c: Equal(g7,g6)
    c: DistanceY(g0,g-3) = 1
    c: DistanceY(g4,g1) = 1
FEATURE [PartDesign::Pocket] Pocket007
  AddSubType = 1
  AlongSketchNormal = false
  AutoTaperInnerAngle = true
  BaseFeature = -> Chamfer002
  CheckUpToFaceLimits = true
  ClaimChildren = false
  Direction = (0,-1,2e-16)
  Fit = 0
  FitJoin = 0
  InnerFit = 0
  InnerFitJoin = 0
  InvalidShape = true
  Length = 0.6
  Length2 = 10
  Linearize = true
  NewSolid = false
  Profile = -> Sketch017
  ReferenceAxis = -> Sketch017 [N_Axis]
  Suppress = false
  TaperInnerAngle = 0
  TaperInnerAngleRev = 0
  TreeRank = 143
  Type = 0
  ValidateShape = true
  _ProfileBasedVersion = 1
  _Version = 1
FEATURE [Sketcher::SketchObject] Sketch018
  ArcFitTolerance = 1e-06
  AttachmentSupport = -> [Pocket007]
  ExternalBSplineMaxDegree = 5
  ExternalBSplineTolerance = 0.0001
  ExternalGeometry = -> [Pocket007]
  FullyConstrained = true
  InternalTolerance = 1e-06
  InvalidShape = false
  MakeInternals = false
  MapMode = 5
  Placement = pos=(-21.4,-8e-16,0) rot=(0.57735,-0.57735,-0.57735;2.0944rad)
  Support = -> [Pocket007]
  TreeRank = 144
  ValidateShape = false
  sketch-geometry (10):
    g0: Circle CenterX=14.8256 CenterY=7.05 CenterZ=0 NormalX=0 NormalY=0 NormalZ=1 AngleXU=0 Radius=1.5
    g1: LineSegment StartX=1.8656 StartY=8.55 StartZ=0 EndX=2.8656 EndY=8.55 EndZ=0
    g2: LineSegment StartX=2.8656 StartY=8.55 StartZ=0 EndX=2.8656 EndY=5.55 EndZ=0
    g3: LineSegment StartX=2.8656 StartY=5.55 StartZ=0 EndX=1.8656 EndY=5.55 EndZ=0
    g4: LineSegment StartX=1.8656 StartY=5.55 StartZ=0 EndX=1.8656 EndY=8.55 EndZ=0
    g5: GeomPoint [constr] X=2.3656 Y=7.05 Z=0
    g6: LineSegment [constr] StartX=2.3656 StartY=7.05 StartZ=0 EndX=5.3656 EndY=14.26 EndZ=0
    g7: LineSegment [constr] StartX=11.8256 StartY=14.26 StartZ=0 EndX=14.8256 EndY=7.05 EndZ=0
    g8: LineSegment [constr] StartX=-21.4 StartY=9.8 StartZ=0 EndX=2.3656 EndY=7.05 EndZ=0
    g9: LineSegment [constr] StartX=2.3656 StartY=7.05 StartZ=0 EndX=-21.4 EndY=4.3 EndZ=0
  constraints (24):
    c: Coincident(g1,g2)
    c: Coincident(g2,g3)
    c: Coincident(g3,g4)
    c: Coincident(g4,g1)
    c: Horizontal(g1)
    c: Horizontal(g3)
    c: Vertical(g2)
    c: Vertical(g4)
    c: Diameter(g0) = 3
    c: DistanceY(g2,g2) = 3
    c: DistanceX(g1,g1) = 1
    c: Symmetric(g1,g2,g5)
    c: Horizontal(g5,g0)
    c: Coincident(g6,g5)
    c: Coincident(g6,g-3)
    c: Coincident(g7,g-4)
    c: Coincident(g7,g0)
    c: Equal(g7,g6)
    c: DistanceX(g-4,g0) = 3
    c: Coincident(g8,g-5)
    c: Coincident(g8,g5)
    c: Coincident(g9,g5)
    c: Coincident(g9,g-6)
    c: Equal(g8,g9)
FEATURE [PartDesign::Pocket] Pocket008
  AddSubType = 1
  AlongSketchNormal = false
  AutoTaperInnerAngle = true
  BaseFeature = -> Pocket007
  CheckUpToFaceLimits = true
  ClaimChildren = false
  Direction = (1,0,0)
  Fit = 0
  FitJoin = 0
  InnerFit = 0
  InnerFitJoin = 0
  InvalidShape = true
  Length = 0.6
  Length2 = 10
  Linearize = true
  NewSolid = false
  Profile = -> Sketch018
  ReferenceAxis = -> Sketch018 [N_Axis]
  Suppress = false
  TaperInnerAngle = 0
  TaperInnerAngleRev = 0
  TreeRank = 145
  Type = 0
  ValidateShape = true
  _ProfileBasedVersion = 1
  _Version = 1
FEATURE [PartDesign::Body] Body001  label="Bottom"
  AutoGroupSolids = false
  ClaimAllChildren = false
  ExportMode = 0
  Group = -> [Import,Sketch001,Pad001,Sketch002,Pad002,Import001,Sketch003,Import002,Import003,Import004,Pocket,Sketch004,Import005,Pocket001,Import006,Sketch006,Pocket002,Sketch007,Pocket003,Sketch008,Pocket004,Sketch009,Pocket005,Fillet001,Fillet002,Sketch015,Pad009,Fillet003,Fillet004,Fillet005,Mirrored003,Chamfer,Chamfer001,Chamfer005,Chamfer002,Sketch017,Pocket007,Sketch018,Pocket008]
  InvalidShape = false
  Origin = -> Origin009
  Tip = -> Pocket008
  TreeRank = 61
  ValidateShape = false
  _ExportChildren = -> [Import,Pad001,Pad002,Import001,Import002,Import003,Import004,Pocket,Import005,Pocket001,Import006,Pocket002,Pocket003,Pocket004,Pocket005,Fillet001,Fillet002,Pad009,Fillet003,Fillet004,Fillet005,Mirrored003,Chamfer,Chamfer001,Chamfer005,Chamfer002,Pocket007,Pocket008]
  _GroupVersion = 1
COMPONENT P2 — recipe-attached ("Switch", modeled in this document).
Construction recipe (the document's own serialized feature program — sketch geometry with constraints, then the solid features built on it; lengths are millimeters unless a unit is written):

FEATURE [Part::SubShapeBinder] Import007  label="Import007(Pocket001)"
  BindCopyOnChange = 0
  BindMode = 0
  ClaimChildren = false
  Context = -> Body002 [Import007.]
  EdgeTolerance = 1e-06
  FillStyle = 0
  Fuse = false
  InvalidShape = false
  MakeFace = false
  MergeEdges = true
  OffsetFill = false
  OffsetIntersection = false
  OffsetJoinType = 0
  OffsetOpenResult = false
  Outline = false
  PartialLoad = false
  Relative = true
  SplitEdges = false
  Support = -> [Body001[Pocket001.]]
  TightBound = false
  TreeRank = 87
  ValidateShape = false
  _Version = 8
FEATURE [Part::SubShapeBinder] Import008  label="Import008(SOLID)"
  BindCopyOnChange = 0
  BindMode = 0
  ClaimChildren = false
  Context = -> Body002 [Import008.]
  EdgeTolerance = 1e-06
  FillStyle = 0
  Fuse = false
  InvalidShape = false
  MakeFace = false
  MergeEdges = true
  OffsetFill = false
  OffsetIntersection = false
  OffsetJoinType = 0
  OffsetOpenResult = false
  Outline = false
  PartialLoad = false
  Relative = true
  SplitEdges = false
  Support = -> [Part007[Part006.Solid002.]]
  TightBound = false
  TreeRank = 89
  ValidateShape = false
  _Version = 8
FEATURE [Sketcher::SketchObject] Sketch005
  ArcFitTolerance = 1e-06
  AttachmentSupport = -> [Import007]
  ExternalBSplineMaxDegree = 5
  ExternalBSplineTolerance = 0.0001
  ExternalGeometry = -> [Import007,Import008]
  FullyConstrained = true
  InternalTolerance = 1e-06
  InvalidShape = false
  MakeInternals = false
  MapMode = 5
  Placement = pos=(0,0,10) rot=(0,0,1;0rad)
  Support = -> [Import007]
  TreeRank = 88
  ValidateShape = false
  sketch-geometry (23):
    g0: LineSegment StartX=-21.8 StartY=-3.7656 StartZ=0 EndX=-21.8 EndY=-5.5656 EndZ=0
    g1: LineSegment StartX=-21.8 StartY=-5.5656 StartZ=0 EndX=-19.8 EndY=-5.5656 EndZ=0
    g2: LineSegment StartX=-19.8 StartY=-5.5656 StartZ=0 EndX=-19.8 EndY=-3.7656 EndZ=0
    g3: LineSegment StartX=-19.8 StartY=-3.7656 StartZ=0 EndX=-18.9744 EndY=-3.7656 EndZ=0
    g4: LineSegment StartX=-18.9744 StartY=-3.7656 StartZ=0 EndX=-18.9744 EndY=-6.1656 EndZ=0
    g5: LineSegment StartX=-18.9744 StartY=-6.1656 StartZ=0 EndX=-17.2744 EndY=-6.1656 EndZ=0
    g6: LineSegment StartX=-17.2744 StartY=-6.1656 StartZ=0 EndX=-17.2744 EndY=-7.1656 EndZ=0
    g7: LineSegment StartX=-17.2744 StartY=-7.1656 StartZ=0 EndX=-18.9744 EndY=-7.1656 EndZ=0
    g8: LineSegment StartX=-18.9744 StartY=-7.1656 StartZ=0 EndX=-18.9744 EndY=-8.8656 EndZ=0
    g9: LineSegment StartX=-18.9744 StartY=-8.8656 StartZ=0 EndX=-17.2744 EndY=-8.8656 EndZ=0
    g10: LineSegment StartX=-17.2744 StartY=-8.8656 StartZ=0 EndX=-17.2744 EndY=-9.8656 EndZ=0
    g11: LineSegment StartX=-17.2744 StartY=-9.8656 StartZ=0 EndX=-18.9744 EndY=-9.8656 EndZ=0
    g12: LineSegment StartX=-18.9744 StartY=-9.8656 StartZ=0 EndX=-18.9744 EndY=-12.2656 EndZ=0
    g13: LineSegment StartX=-18.9744 StartY=-12.2656 StartZ=0 EndX=-19.8 EndY=-12.2656 EndZ=0
    g14: LineSegment StartX=-19.8 StartY=-12.2656 StartZ=0 EndX=-19.8 EndY=-10.4656 EndZ=0
    g15: LineSegment StartX=-19.8 StartY=-10.4656 StartZ=0 EndX=-21.8 EndY=-10.4656 EndZ=0
    g16: LineSegment StartX=-21.8 StartY=-10.4656 StartZ=0 EndX=-21.8 EndY=-12.2656 EndZ=0
    g17: LineSegment StartX=-21.8 StartY=-3.7656 StartZ=0 EndX=-22.2 EndY=-3.7656 EndZ=0
    g18: LineSegment StartX=-22.2 StartY=-12.2656 StartZ=0 EndX=-21.8 EndY=-12.2656 EndZ=0
    g19: LineSegment StartX=-22.2 StartY=-3.7656 StartZ=0 EndX=-22.7 EndY=-7.2656 EndZ=0
    g20: LineSegment StartX=-22.7 StartY=-7.2656 StartZ=0 EndX=-23.7 EndY=-8.0156 EndZ=0
    g21: LineSegment StartX=-23.7 StartY=-8.0156 StartZ=0 EndX=-22.7 EndY=-8.7656 EndZ=0
    g22: LineSegment StartX=-22.7 StartY=-8.7656 StartZ=0 EndX=-22.2 EndY=-12.2656 EndZ=0
  constraints (69):
    c: Vertical(g0)
    c: Coincident(g0,g1)
    c: Horizontal(g1)
    c: Coincident(g1,g2)
    c: Vertical(g2)
    c: Coincident(g2,g3)
    c: Horizontal(g3)
    c: Coincident(g3,g4)
    c: Vertical(g4)
    c: Coincident(g4,g5)
    c: Horizontal(g5)
    c: Coincident(g5,g6)
    c: Vertical(g6)
    c: Coincident(g6,g7)
    c: Horizontal(g7)
    c: Coincident(g7,g8)
    c: Vertical(g8)
    c: Coincident(g8,g9)
    c: Horizontal(g9)
    c: Coincident(g9,g10)
    c: Vertical(g10)
    c: Coincident(g10,g11)
    c: Horizontal(g11)
    c: Coincident(g11,g12)
    c: Vertical(g12)
    c: Coincident(g12,g13)
    c: Horizontal(g13)
    c: Coincident(g13,g14)
    c: Vertical(g14)
    c: Coincident(g14,g15)
    c: Horizontal(g15)
    c: Coincident(g15,g16)
    c: Vertical(g16)
    c: Horizontal(g16,g13)
    c: Horizontal(g0,g2)
    c: Equal(g16,g0)
    c: Equal(g1,g15)
    c: Vertical(g4,g7)
    c: Vertical(g8,g11)
    c: Equal(g9,g7)
    c: Equal(g6,g10)
    c: DistanceY(g10,g10) = 1
    c: DistanceY(g-5,g7) = 0.2
    c: DistanceY(g8,g-6) = 0.2
    c: DistanceX(g7,g-7) = 0.5
    c: Vertical(g-5,g6)
    c: DistanceY(g1,g-3) = 0.2
    c: DistanceX(g-3,g1) = 0.4
    c: DistanceX(g0,g-3) = 0.4
    c: Equal(g12,g4)
    c: DistanceY(g14,g14) = 1.8
    c: Coincident(g0,g17)
    c: Horizontal(g17)
    c: Coincident(g18,g16)
    c: Horizontal(g18)
    c: Equal(g18,g17)
    c: DistanceX(g17,g17) = 0.4
    c: Vertical(g0,g15)
    c: Coincident(g17,g19)
    c: Coincident(g19,g20)
    c: Coincident(g20,g21)
    c: Coincident(g21,g22)
    c: Coincident(g22,g18)
    c: Equal(g22,g19)
    c: Equal(g20,g21)
    c: Vertical(g19,g21)
    c: DistanceX(g19,g17) = 0.5
    c: DistanceX(g20,g19) = 1
    c: DistanceY(g21,g19) = 1.5
FEATURE [PartDesign::SubShapeBinder] Import009  label="Import009(Pocket001)"
  BindCopyOnChange = 0
  BindMode = 0
  ClaimChildren = false
  Context = -> Body002 [Import009.]
  EdgeTolerance = 1e-06
  FillStyle = 0
  Fuse = false
  InvalidShape = false
  MakeFace = false
  MergeEdges = true
  OffsetFill = false
  OffsetIntersection = false
  OffsetJoinType = 0
  OffsetOpenResult = false
  Outline = false
  PartialLoad = false
  Relative = true
  SplitEdges = false
  Support = -> [Body001[Pocket001.Face14]]
  TightBound = false
  TreeRank = 91
  ValidateShape = false
  _Version = 8
FEATURE [PartDesign::Pad] Pad003
  AddSubType = 0
  AlongSketchNormal = false
  AutoTaperInnerAngle = true
  CheckUpToFaceLimits = true
  ClaimChildren = false
  Direction = (0,0,1)
  Fit = 0
  FitJoin = 0
  InnerFit = 0
  InnerFitJoin = 0
  InvalidShape = false
  Length = 10
  Length2 = 10
  Linearize = true
  NewSolid = false
  Offset = 0.2
  Profile = -> Sketch005
  ReferenceAxis = -> Sketch005 [N_Axis]
  Suppress = false
  TaperInnerAngle = 0
  TaperInnerAngleRev = 0
  TreeRank = 90
  Type = 3
  UpToFace = -> Import009
  ValidateShape = false
  _ProfileBasedVersion = 1
FEATURE [PartDesign::Body] Body002  label="Switch"
  AutoGroupSolids = false
  ClaimAllChildren = false
  ExportMode = 0
  Group = -> [Import007,Sketch005,Import008,Pad003,Import009]
  InvalidShape = false
  Origin = -> Origin010
  Tip = -> Pad003
  TreeRank = 86
  ValidateShape = false
  _ExportChildren = -> [Import007,Import008,Pad003,Import009]
  _GroupVersion = 1
COMPONENT P3 — recipe-attached ("Top", modeled in this document).
Construction recipe (the document's own serialized feature program — sketch geometry with constraints, then the solid features built on it; lengths are millimeters unless a unit is written):

FEATURE [Part::SubShapeBinder] Import010  label="Import010(Pocket005)"
  BindCopyOnChange = 0
  BindMode = 0
  ClaimChildren = false
  Context = -> Body003 [Import010.]
  EdgeTolerance = 1e-06
  FillStyle = 0
  Fuse = false
  InvalidShape = false
  MakeFace = false
  MergeEdges = true
  OffsetFill = false
  OffsetIntersection = false
  OffsetJoinType = 0
  OffsetOpenResult = false
  Outline = false
  PartialLoad = false
  Relative = true
  SplitEdges = false
  Support = -> [Body001[Pocket005.]]
  TightBound = false
  TreeRank = 110
  ValidateShape = false
  _Version = 8
FEATURE [Sketcher::SketchObject] Sketch010
  ArcFitTolerance = 1e-06
  AttachmentSupport = -> [Import010]
  ExternalBSplineMaxDegree = 5
  ExternalBSplineTolerance = 0.0001
  ExternalGeometry = -> [Import010]
  FullyConstrained = true
  InternalTolerance = 1e-06
  InvalidShape = false
  MakeInternals = false
  MapMode = 5
  Placement = pos=(0,-3.1e-15,14.26) rot=(0,0,1;0rad)
  Support = -> [Import010]
  TreeRank = 111
  ValidateShape = false
  sketch-geometry (4):
    g0: LineSegment StartX=-21.4 StartY=21.4 StartZ=0 EndX=21.4 EndY=21.4 EndZ=0
    g1: LineSegment StartX=21.4 StartY=21.4 StartZ=0 EndX=21.4 EndY=-21.4 EndZ=0
    g2: LineSegment StartX=21.4 StartY=-21.4 StartZ=0 EndX=-21.4 EndY=-21.4 EndZ=0
    g3: LineSegment StartX=-21.4 StartY=-21.4 StartZ=0 EndX=-21.4 EndY=21.4 EndZ=0
  constraints (10):
    c: Coincident(g0,g1)
    c: Coincident(g1,g2)
    c: Coincident(g2,g3)
    c: Coincident(g3,g0)
    c: Horizontal(g0)
    c: Horizontal(g2)
    c: Vertical(g1)
    c: Vertical(g3)
    c: Coincident(g0,g-3)
    c: Coincident(g1,g-4)
FEATURE [PartDesign::Pad] Pad004
  AddSubType = 0
  AlongSketchNormal = false
  AutoTaperInnerAngle = true
  CheckUpToFaceLimits = true
  ClaimChildren = false
  Direction = (0,-2e-16,1)
  Fit = 0
  FitJoin = 0
  InnerFit = 0
  InnerFitJoin = 0
  InvalidShape = false
  Length = 1.2
  Length2 = 10
  Linearize = true
  NewSolid = false
  Profile = -> Sketch010
  ReferenceAxis = -> Sketch010 [N_Axis]
  Suppress = false
  TaperInnerAngle = 0
  TaperInnerAngleRev = 0
  TreeRank = 112
  Type = 0
  ValidateShape = false
  _ProfileBasedVersion = 1
FEATURE [Sketcher::SketchObject] Sketch011
  ArcFitTolerance = 1e-06
  AttachmentSupport = -> [Pad004]
  ExternalBSplineMaxDegree = 5
  ExternalBSplineTolerance = 0.0001
  ExternalGeometry = -> [Pad004,Import010]
  FullyConstrained = true
  InternalTolerance = 1e-06
  InvalidShape = false
  MakeInternals = false
  MapMode = 5
  Placement = pos=(0,-3.6e-15,14.26) rot=(1,0,0;3.14159rad)
  Support = -> [Pad004]
  TreeRank = 113
  ValidateShape = false
  sketch-geometry (18):
    g0: LineSegment StartX=-20.2 StartY=17.2 StartZ=0 EndX=-17.2 EndY=17.2 EndZ=0
    g1: LineSegment StartX=-17.2 StartY=17.2 StartZ=0 EndX=-17.2 EndY=14.2 EndZ=0
    g2: LineSegment StartX=-17.2 StartY=14.2 StartZ=0 EndX=-20.2 EndY=14.2 EndZ=0
    g3: LineSegment StartX=-20.2 StartY=14.2 StartZ=0 EndX=-20.2 EndY=17.2 EndZ=0
    g4: LineSegment StartX=20.2 StartY=17.2 StartZ=0 EndX=17.2 EndY=17.2 EndZ=0
    g5: LineSegment StartX=17.2 StartY=17.2 StartZ=0 EndX=17.2 EndY=14.2 EndZ=0
    g6: LineSegment StartX=17.2 StartY=14.2 StartZ=0 EndX=20.2 EndY=14.2 EndZ=0
    g7: LineSegment StartX=20.2 StartY=14.2 StartZ=0 EndX=20.2 EndY=17.2 EndZ=0
    g8: LineSegment StartX=20.2 StartY=-17.2 StartZ=0 EndX=17.2 EndY=-17.2 EndZ=0
    g9: LineSegment StartX=17.2 StartY=-17.2 StartZ=0 EndX=17.2 EndY=-14.2 EndZ=0
    g10: LineSegment StartX=17.2 StartY=-14.2 StartZ=0 EndX=20.2 EndY=-14.2 EndZ=0
    g11: LineSegment StartX=20.2 StartY=-14.2 StartZ=0 EndX=20.2 EndY=-17.2 EndZ=0
    g12: LineSegment StartX=-20.2 StartY=-17.2 StartZ=0 EndX=-17.2 EndY=-17.2 EndZ=0
    g13: LineSegment StartX=-17.2 StartY=-17.2 StartZ=0 EndX=-17.2 EndY=-14.2 EndZ=0
    g14: LineSegment StartX=-17.2 StartY=-14.2 StartZ=0 EndX=-20.2 EndY=-14.2 EndZ=0
    g15: LineSegment StartX=-20.2 StartY=-14.2 StartZ=0 EndX=-20.2 EndY=-17.2 EndZ=0
    g16: LineSegment [constr] StartX=-20.2 StartY=-20.2 StartZ=0 EndX=-17.2 EndY=-17.2 EndZ=0
    g17: LineSegment [constr] StartX=-20.2 StartY=20.2 StartZ=0 EndX=-17.2 EndY=17.2 EndZ=0
  constraints (52):
    c: Coincident(g0,g1)
    c: Coincident(g1,g2)
    c: Coincident(g2,g3)
    c: Coincident(g3,g0)
    c: Horizontal(g0)
    c: Horizontal(g2)
    c: Vertical(g1)
    c: Vertical(g3)
    c: PointOnObject(g0,g-5)
    c: Coincident(g4,g5)
    c: Coincident(g5,g6)
    c: Coincident(g6,g7)
    c: Coincident(g7,g4)
    c: Horizontal(g4)
    c: Horizontal(g6)
    c: Vertical(g5)
    c: Vertical(g7)
    c: PointOnObject(g4,g-6)
    c: Coincident(g8,g9)
    c: Coincident(g9,g10)
    c: Coincident(g10,g11)
    c: Coincident(g11,g8)
    c: Horizontal(g8)
    c: Horizontal(g10)
    c: Vertical(g9)
    c: Vertical(g11)
    c: Coincident(g12,g13)
    c: Coincident(g13,g14)
    c: Coincident(g14,g15)
    c: Coincident(g15,g12)
    c: Horizontal(g12)
    c: Horizontal(g14)
    c: Vertical(g13)
    c: Vertical(g15)
    c: PointOnObject(g12,g-7)
    c: PointOnObject(g8,g-6)
    c: Horizontal(g12,g8)
    c: Horizontal(g1,g5)
    c: Equal(g1,g5)
    c: Equal(g5,g9)
    c: Equal(g9,g13)
    c: Equal(g14,g10)
    c: Equal(g10,g4)
    c: Equal(g4,g0)
    c: Coincident(g16,g-7)
    c: Coincident(g16,g12)
    c: Coincident(g17,g-5)
    c: Coincident(g17,g0)
    c: Equal(g17,g16)
    c: DistanceY(g13,g13) = 3
    c: DistanceX(g14,g14) = 3
    c: DistanceY(g-7,g12) = 3
FEATURE [PartDesign::Pad] Pad005
  AddSubType = 0
  AlongSketchNormal = false
  AutoTaperInnerAngle = true
  BaseFeature = -> Pad004
  CheckUpToFaceLimits = true
  ClaimChildren = false
  Direction = (0,2e-16,-1)
  Fit = 0
  FitJoin = 0
  InnerFit = 0
  InnerFitJoin = 0
  InvalidShape = false
  Length = 3
  Length2 = 10
  Linearize = true
  NewSolid = false
  Profile = -> Sketch011
  ReferenceAxis = -> Sketch011 [N_Axis]
  Suppress = false
  TaperInnerAngle = 0
  TaperInnerAngleRev = 0
  TreeRank = 114
  Type = 0
  ValidateShape = false
  _ProfileBasedVersion = 1
FEATURE [Sketcher::SketchObject] Sketch012
  ArcFitTolerance = 1e-06
  AttachmentSupport = -> [Pad005]
  ExternalBSplineMaxDegree = 5
  ExternalBSplineTolerance = 0.0001
  ExternalGeometry = -> [Pad005]
  FullyConstrained = true
  InternalTolerance = 1e-06
  InvalidShape = false
  MakeInternals = false
  MapMode = 5
  Placement = pos=(0,17.2,4.3e-15) rot=(0,0.707107,0.707107;3.14159rad)
  Support = -> [Pad005]
  TreeRank = 115
  ValidateShape = false
  sketch-geometry (3):
    g0: LineSegment StartX=-20.2 StartY=11.26 StartZ=0 EndX=-20.9002 EndY=12.26 EndZ=0
    g1: LineSegment StartX=-20.9002 StartY=12.26 StartZ=0 EndX=-20.2 EndY=13.26 EndZ=0
    g2: LineSegment StartX=-20.2 StartY=13.26 StartZ=0 EndX=-20.2 EndY=11.26 EndZ=0
  constraints (8):
    c: Coincident(g-3,g0)
    c: Coincident(g0,g1)
    c: PointOnObject(g1,g-3)
    c: Coincident(g1,g2)
    c: Coincident(g2,g0)
    c: DistanceY(g2,g2) = 2
    c: Equal(g1,g0)
    c: Angle(g0,g1) = 1.91986
FEATURE [PartDesign::Pad] Pad006
  AddSubType = 0
  AlongSketchNormal = false
  AutoTaperInnerAngle = true
  BaseFeature = -> Pad005
  CheckUpToFaceLimits = true
  ClaimChildren = false
  Direction = (0,1,2e-16)
  Fit = 0
  FitJoin = 0
  InnerFit = 0
  InnerFitJoin = 0
  InvalidShape = false
  Length = 10
  Length2 = 10
  Linearize = true
  NewSolid = false
  Profile = -> Sketch012
  ReferenceAxis = -> Sketch012 [N_Axis]
  Reversed = true
  Suppress = false
  TaperInnerAngle = 0
  TaperInnerAngleRev = 0
  TreeRank = 116
  Type = 3
  UpToFace = -> Pad005 [Face13]
  ValidateShape = false
  _ProfileBasedVersion = 1
FEATURE [PartDesign::Mirrored] Mirrored
  AddSubType = 0
  CopyShape = false
  InvalidShape = false
  MirrorPlane = -> Sketch012 [V_Axis]
  NewSolid = false
  ParallelTransform = true
  SubTransform = true
  Suppress = false
  TreeRank = 118
  ValidateShape = false
  _Version = 3
FEATURE [PartDesign::Mirrored] Mirrored001
  AddSubType = 0
  CopyShape = false
  InvalidShape = false
  MirrorPlane = -> XZ_Plane003
  NewSolid = false
  ParallelTransform = true
  SubTransform = true
  Suppress = false
  TreeRank = 119
  ValidateShape = false
  _Version = 3
FEATURE [PartDesign::MultiTransform] MultiTransform
  AddSubType = 0
  BaseFeature = -> Pad006
  CopyShape = false
  InvalidShape = false
  NewSolid = false
  OriginalSubs = -> [Pad006]
  Originals = -> [Pad006]
  ParallelTransform = true
  SubTransform = true
  Suppress = false
  Transformations = -> [Mirrored,Mirrored001]
  TreeRank = 117
  ValidateShape = false
  _Version = 3
FEATURE [Sketcher::SketchObject] Sketch013
  ArcFitTolerance = 1e-06
  AttachmentSupport = -> [MultiTransform]
  ExternalBSplineMaxDegree = 5
  ExternalBSplineTolerance = 0.0001
  ExternalGeometry = -> [Import010]
  FullyConstrained = true
  InternalTolerance = 1e-06
  InvalidShape = false
  MakeInternals = false
  MapMode = 5
  Placement = pos=(0,-3.6e-15,14.26) rot=(1,0,0;3.14159rad)
  Support = -> [MultiTransform]
  TreeRank = 120
  ValidateShape = false
  sketch-geometry (10):
    g0: LineSegment StartX=-2.28331 StartY=-17.2 StartZ=0 EndX=1.71669 EndY=-17.2 EndZ=0
    g1: LineSegment StartX=1.71669 StartY=-17.2 StartZ=0 EndX=1.71669 EndY=-20.2 EndZ=0
    g2: LineSegment StartX=1.71669 StartY=-20.2 StartZ=0 EndX=-2.28331 EndY=-20.2 EndZ=0
    g3: LineSegment StartX=-2.28331 StartY=-20.2 StartZ=0 EndX=-2.28331 EndY=-17.2 EndZ=0
    g4: LineSegment StartX=-2.28331 StartY=20.2 StartZ=0 EndX=1.71669 EndY=20.2 EndZ=0
    g5: LineSegment StartX=1.71669 StartY=20.2 StartZ=0 EndX=1.71669 EndY=17.2 EndZ=0
    g6: LineSegment StartX=1.71669 StartY=17.2 StartZ=0 EndX=-2.28331 EndY=17.2 EndZ=0
    g7: LineSegment StartX=-2.28331 StartY=17.2 StartZ=0 EndX=-2.28331 EndY=20.2 EndZ=0
    g8: LineSegment [constr] StartX=-6.18774 StartY=-20.2 StartZ=0 EndX=-2.28331 EndY=-17.2 EndZ=0
    g9: LineSegment [constr] StartX=1.71669 StartY=-17.2 StartZ=0 EndX=5.62112 EndY=-20.2 EndZ=0
  constraints (28):
    c: Coincident(g0,g1)
    c: Coincident(g1,g2)
    c: Coincident(g2,g3)
    c: Coincident(g3,g0)
    c: Horizontal(g0)
    c: Horizontal(g2)
    c: Vertical(g1)
    c: Vertical(g3)
    c: Coincident(g4,g5)
    c: Coincident(g5,g6)
    c: Coincident(g6,g7)
    c: Coincident(g7,g4)
    c: Horizontal(g4)
    c: Horizontal(g6)
    c: Vertical(g5)
    c: Vertical(g7)
    c: PointOnObject(g2,g-4)
    c: PointOnObject(g4,g-3)
    c: Equal(g7,g3)
    c: Equal(g0,g6)
    c: DistanceX(g6,g6) = 4
    c: DistanceY(g7,g7) = 3
    c: Vertical(g0,g6)
    c: Coincident(g8,g-4)
    c: Coincident(g8,g0)
    c: Coincident(g9,g0)
    c: Coincident(g9,g-4)
    c: Equal(g9,g8)
FEATURE [PartDesign::Pad] Pad007
  AddSubType = 0
  AlongSketchNormal = false
  AutoTaperInnerAngle = true
  BaseFeature = -> MultiTransform
  CheckUpToFaceLimits = true
  ClaimChildren = false
  Direction = (0,2e-16,-1)
  Fit = 0
  FitJoin = 0
  InnerFit = 0
  InnerFitJoin = 0
  InvalidShape = false
  Length = 3
  Length2 = 10
  Linearize = true
  NewSolid = false
  Profile = -> Sketch013
  ReferenceAxis = -> Sketch013 [N_Axis]
  Suppress = false
  TaperInnerAngle = 0
  TaperInnerAngleRev = 0
  TreeRank = 121
  Type = 0
  ValidateShape = false
  _ProfileBasedVersion = 1
FEATURE [Sketcher::SketchObject] Sketch014
  ArcFitTolerance = 1e-06
  AttachmentSupport = -> [Pad007]
  ExternalBSplineMaxDegree = 5
  ExternalBSplineTolerance = 0.0001
  ExternalGeometry = -> [Pad007]
  FullyConstrained = true
  InternalTolerance = 1e-06
  InvalidShape = false
  MakeInternals = false
  MapMode = 5
  Placement = pos=(1.71669,0,0) rot=(0.57735,0.57735,0.57735;2.0944rad)
  Support = -> [Pad007]
  TreeRank = 122
  ValidateShape = false
  sketch-geometry (3):
    g0: LineSegment StartX=-20.2 StartY=11.26 StartZ=0 EndX=-20.9002 EndY=12.26 EndZ=0
    g1: LineSegment StartX=-20.9002 StartY=12.26 StartZ=0 EndX=-20.2 EndY=13.26 EndZ=0
    g2: LineSegment StartX=-20.2 StartY=13.26 StartZ=0 EndX=-20.2 EndY=11.26 EndZ=0
  constraints (8):
    c: Coincident(g-3,g0)
    c: Coincident(g0,g1)
    c: PointOnObject(g1,g-3)
    c: Coincident(g1,g2)
    c: Coincident(g2,g0)
    c: Equal(g0,g1)
    c: Angle(g0,g1) = 1.91986
    c: DistanceY(g2,g2) = 2
FEATURE [PartDesign::Pad] Pad008
  AddSubType = 0
  AlongSketchNormal = false
  AutoTaperInnerAngle = true
  BaseFeature = -> Pad007
  CheckUpToFaceLimits = true
  ClaimChildren = false
  Direction = (1,0,0)
  Fit = 0
  FitJoin = 0
  InnerFit = 0
  InnerFitJoin = 0
  InvalidShape = false
  Length = 10
  Length2 = 10
  Linearize = true
  NewSolid = false
  Profile = -> Sketch014
  ReferenceAxis = -> Sketch014 [N_Axis]
  Suppress = false
  TaperInnerAngle = 0
  TaperInnerAngleRev = 0
  TreeRank = 123
  Type = 3
  UpToFace = -> Pad007 [Face18]
  ValidateShape = false
  _ProfileBasedVersion = 1
FEATURE [PartDesign::Mirrored] Mirrored002
  AddSubType = 0
  BaseFeature = -> Pad008
  CopyShape = false
  InvalidShape = false
  MirrorPlane = -> XZ_Plane003
  NewSolid = false
  OriginalSubs = -> [Pad008]
  Originals = -> [Pad008]
  ParallelTransform = true
  SubTransform = true
  Suppress = false
  TreeRank = 124
  ValidateShape = false
  _Version = 3
FEATURE [PartDesign::Fillet] Fillet
  AddSubType = 0
  Base = -> Mirrored002 [Edge111,Edge99,Edge107,Edge125,Edge129,Edge119]
  BaseFeature = -> Mirrored002
  InvalidShape = false
  NewSolid = false
  Radius = 0.1
  SupportTransform = false
  Suppress = false
  TreeRank = 125
  UseAllEdges = false
  ValidateShape = false
FEATURE [PartDesign::Fillet] Fillet006
  AddSubType = 0
  Base = -> Fillet [Edge49,Edge53,Edge48,Edge51]
  BaseFeature = -> Fillet
  InvalidShape = false
  NewSolid = false
  Radius = 4
  SupportTransform = false
  Suppress = false
  TreeRank = 137
  UseAllEdges = false
  ValidateShape = true
FEATURE [Sketcher::SketchObject] Sketch016
  ArcFitTolerance = 1e-06
  AttachmentSupport = -> [Fillet006]
  ExternalBSplineMaxDegree = 5
  ExternalBSplineTolerance = 0.0001
  ExternalGeometry = -> [Fillet006]
  FullyConstrained = true
  InternalTolerance = 1e-06
  InvalidShape = false
  MakeInternals = false
  MapMode = 5
  Placement = pos=(0,-3.8e-15,15.46) rot=(0,0,1;0rad)
  Support = -> [Fillet006]
  TreeRank = 138
  ValidateShape = false
  sketch-geometry (10):
    g0: ArcOfCircle CenterX=-11.4 CenterY=11.4 CenterZ=0 NormalX=0 NormalY=0 NormalZ=1 AngleXU=0 Radius=5 StartAngle=1.5708 EndAngle=3.14159
    g1: LineSegment StartX=-11.4 StartY=16.4 StartZ=0 EndX=11.4 EndY=16.4 EndZ=0
    g2: ArcOfCircle CenterX=11.4 CenterY=11.4 CenterZ=0 NormalX=0 NormalY=0 NormalZ=1 AngleXU=0 Radius=5 StartAngle=0 EndAngle=1.5708
    g3: LineSegment StartX=16.4 StartY=11.4 StartZ=0 EndX=16.4 EndY=-11.4 EndZ=0
    g4: ArcOfCircle CenterX=11.4 CenterY=-11.4 CenterZ=0 NormalX=0 NormalY=0 NormalZ=1 AngleXU=0 Radius=5 StartAngle=4.71239 EndAngle=6.28319
    g5: LineSegment StartX=11.4 StartY=-16.4 StartZ=0 EndX=-11.4 EndY=-16.4 EndZ=0
    g6: ArcOfCircle CenterX=-11.4 CenterY=-11.4 CenterZ=0 NormalX=0 NormalY=0 NormalZ=1 AngleXU=0 Radius=5 StartAngle=3.14159 EndAngle=4.71239
    g7: LineSegment StartX=-16.4 StartY=-11.4 StartZ=0 EndX=-16.4 EndY=11.4 EndZ=0
    g8: GeomPoint [constr] X=-16.4 Y=16.4 Z=0
    g9: GeomPoint [constr] X=16.4 Y=-16.4 Z=0
  constraints (23):
    c: Tangent(g0,g1) = 1.5708
    c: Tangent(g1,g2) = 1.5708
    c: Tangent(g2,g3) = 1.5708
    c: Tangent(g3,g4) = 1.5708
    c: Tangent(g4,g5) = 1.5708
    c: Tangent(g5,g6) = 1.5708
    c: Tangent(g6,g7) = 1.5708
    c: Tangent(g7,g0) = 1.5708
    c: Horizontal(g1)
    c: Horizontal(g5)
    c: Vertical(g3)
    c: Vertical(g7)
    c: Equal(g0,g2)
    c: Equal(g2,g4)
    c: Equal(g4,g6)
    c: PointOnObject(g8,g1)
    c: PointOnObject(g8,g7)
    c: PointOnObject(g9,g3)
    c: PointOnObject(g9,g5)
    c: Symmetric(g8,g9,g-1)
    c: Equal(g3,g1)
    c: DistanceY(g0,g-3) = 5
    c: Radius(g0) = 5
FEATURE [PartDesign::Pocket] Pocket006
  AddSubType = 1
  AlongSketchNormal = false
  AutoTaperInnerAngle = true
  BaseFeature = -> Fillet006
  CheckUpToFaceLimits = true
  ClaimChildren = false
  Direction = (0,2e-16,-1)
  Fit = 0
  FitJoin = 0
  InnerFit = 0
  InnerFitJoin = 0
  InvalidShape = false
  Length = 5
  Length2 = 10
  Linearize = true
  NewSolid = false
  Profile = -> Sketch016
  ReferenceAxis = -> Sketch016 [N_Axis]
  Suppress = false
  TaperInnerAngle = 0
  TaperInnerAngleRev = 0
  TreeRank = 139
  Type = 1
  ValidateShape = true
  _ProfileBasedVersion = 1
  _Version = 1
FEATURE [PartDesign::Chamfer] Chamfer003
  AddSubType = 0
  Angle = 45
  Base = -> Pocket006 [Edge51,Edge74]
  BaseFeature = -> Pocket006
  ChamferType = 0
  FlipDirection = false
  InvalidShape = false
  NewSolid = false
  Size = 1
  Size2 = 1
  SupportTransform = false
  Suppress = false
  TreeRank = 140
  UseAllEdges = false
  ValidateShape = true
FEATURE [PartDesign::Chamfer] Chamfer004
  AddSubType = 0
  Angle = 45
  Base = -> Chamfer003 [Edge135,Edge152,Edge110,Edge86,Edge122,Edge130]
  BaseFeature = -> Chamfer003
  ChamferType = 0
  FlipDirection = false
  InvalidShape = false
  NewSolid = false
  Size = 2
  Size2 = 1
  SupportTransform = false
  Suppress = false
  TreeRank = 141
  UseAllEdges = false
  ValidateShape = true
FEATURE [PartDesign::Body] Body003  label="Top"
  AutoGroupSolids = false
  ClaimAllChildren = false
  ExportMode = 0
  Group = -> [Import010,Sketch010,Pad004,Sketch011,Pad005,Sketch012,Pad006,MultiTransform,Mirrored,Mirrored001,Sketch013,Pad007,Sketch014,Pad008,Mirrored002,Fillet,Fillet006,Sketch016,Pocket006,Chamfer003,Chamfer004]
  InvalidShape = false
  Origin = -> Origin011
  Tip = -> Chamfer004
  TreeRank = 109
  ValidateShape = false
  _ExportChildren = -> [Import010,Pad004,Pad005,Pad006,MultiTransform,Pad007,Pad008,Mirrored002,Fillet,Fillet006,Pocket006,Chamfer003,Chamfer004]
  _GroupVersion = 1
COMPONENT P4 — geometry summary ("PCB"; no construction recipe available for this part):
  bounding box: 41.1 x 40.0 x 5.0 mm
  tessellated surface: 77,588 triangles
  volume: 2674 mm^3 (33% of its bounding box)
PROVENANCE & LICENSES
A FreeCAD (.FCStd) document from a public repository crawl; recipes are the document's own serialized feature recipes (and, for linked parts, companion documents' recipes).
License: mit.
